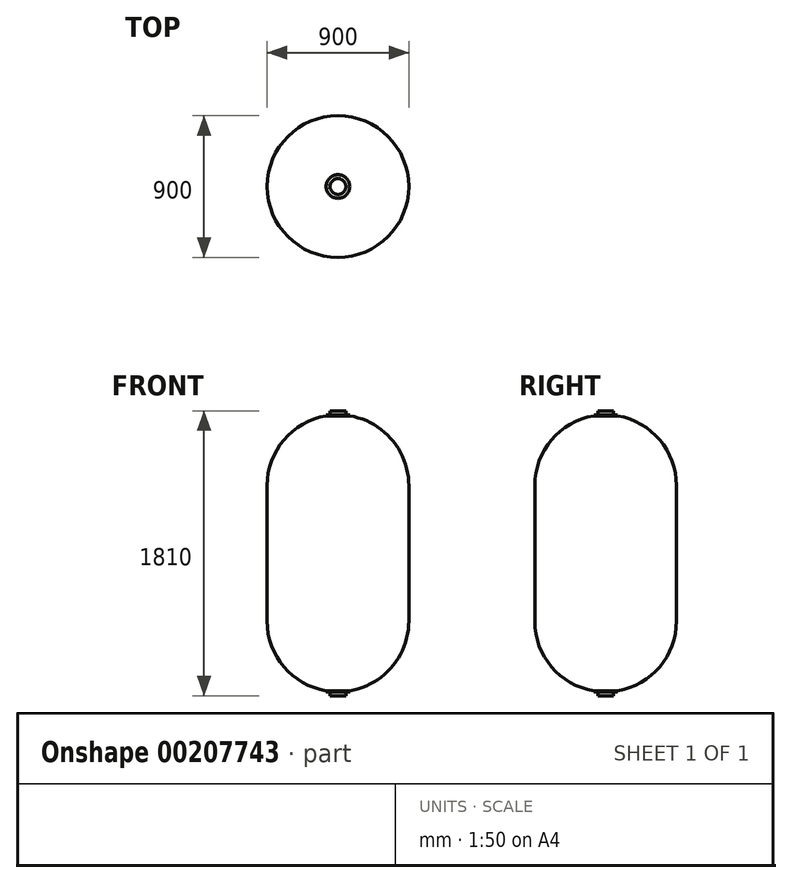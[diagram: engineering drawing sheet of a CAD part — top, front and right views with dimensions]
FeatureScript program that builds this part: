
annotation { "Feature Type Name" : "Feature", "Feature Type Description" : "" }
export const myFeature = defineFeature(function(context is Context, id is Id, definition is map)
    precondition{}
    {
        {
            var Q0;
            Q0=qCreatedBy(makeId("Front.planeOp"),FACE);
            var sketch = newSketch(context, id + "F0", { "sketchPlane" : qUnion([Q0])});
            skArc(sketch, "E0", {"start": v(75, 6.3) * mm, "mid": v(343.7, 159.53) * mm, "end": v(450, 450) * mm});
            skLineSegment(sketch, "E1", {"start": v(450, 450) * mm, "end": v(450, 1310) * mm});
            skArc(sketch, "E2", {"start": v(450, 1310) * mm, "mid": v(343.7, 1600.47) * mm, "end": v(75, 1753.7) * mm});
            skLineSegment(sketch, "E3", {"start": v(0, 1760) * mm, "end": v(0, 0) * mm});
            skLineSegment(sketch, "E4", {"start": v(75, 6.3) * mm, "end": v(75, 0) * mm});
            skLineSegment(sketch, "E5", {"start": v(75, 0) * mm, "end": v(50, 0) * mm});
            skLineSegment(sketch, "E6", {"start": v(50, 0) * mm, "end": v(50, -25) * mm});
            skLineSegment(sketch, "E7", {"start": v(50, -25) * mm, "end": v(0, -25) * mm});
            skLineSegment(sketch, "E8", {"start": v(0, -25) * mm, "end": v(0, 0) * mm});
            skLineSegment(sketch, "E9", {"start": v(75, 1753.7) * mm, "end": v(75, 1760) * mm});
            skLineSegment(sketch, "E10", {"start": v(75, 1760) * mm, "end": v(50, 1760) * mm});
            skLineSegment(sketch, "E11", {"start": v(50, 1760) * mm, "end": v(50, 1785) * mm});
            skLineSegment(sketch, "E12", {"start": v(50, 1785) * mm, "end": v(0, 1785) * mm});
            skLineSegment(sketch, "E13", {"start": v(0, 1785) * mm, "end": v(0, 1760) * mm});
            skSolve(sketch);
        }
        {
            var Q0;
            Q0=makeQuery(id+"F0.imprint","IMPRINT",FACE,{"disambiguationData":[TD([[makeQuery(id+"F0.imprint","IMPRINT",EDGE,{"derivedFrom":sQuery(id+"F0.wireOp",EDGE,"E0")}),1.0]])]});
            var Q1;
            Q1=sQuery(id+"F0.wireOp",EDGE,"E3");
            revolve(context, id + "F1", {"entities" : qUnion([Q0]), "axis" : qUnion([Q1]), "revolveType" : RevolveType.FULL});
        }
    });
